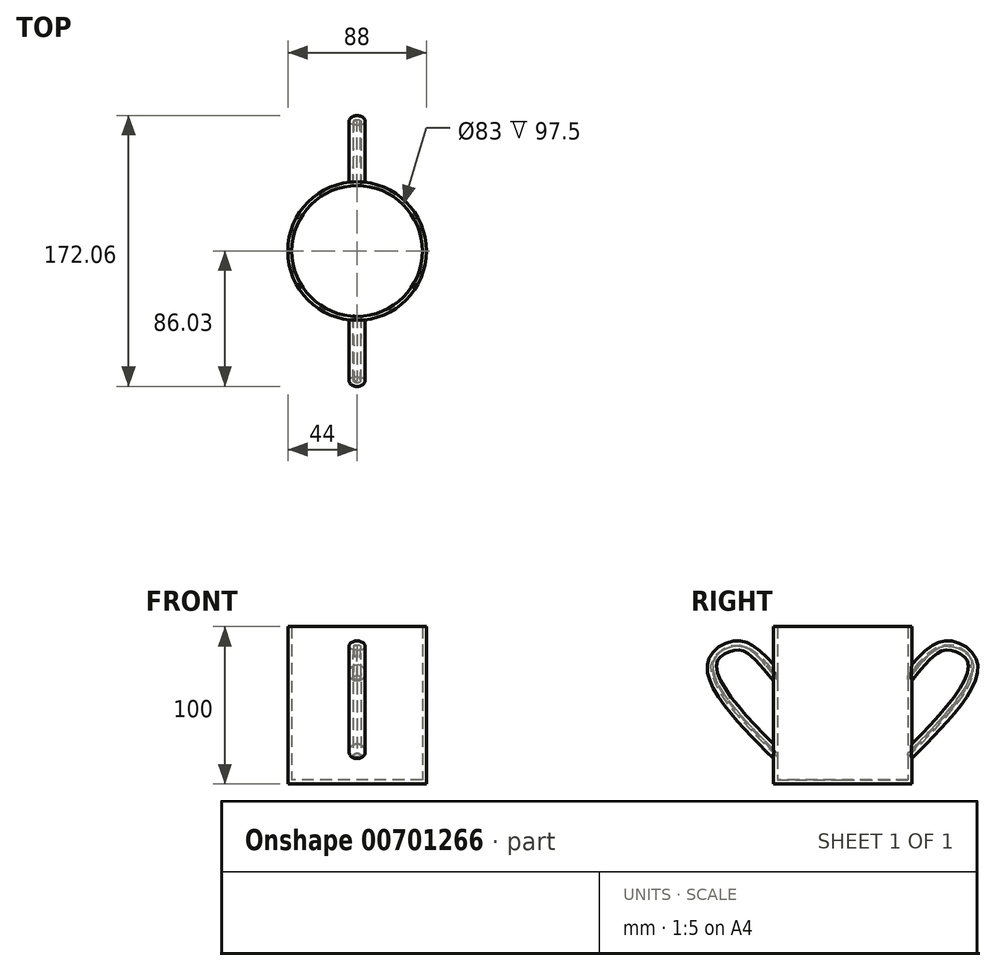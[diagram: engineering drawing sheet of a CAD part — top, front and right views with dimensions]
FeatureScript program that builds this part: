
annotation { "Feature Type Name" : "Feature", "Feature Type Description" : "" }
export const myFeature = defineFeature(function(context is Context, id is Id, definition is map)
    precondition{}
    {
        {
            var Q0;
            Q0=qCreatedBy(makeId("Top.planeOp"),FACE);
            var sketch = newSketch(context, id + "F0", { "sketchPlane" : qUnion([Q0])});
            skCircle(sketch, "E0", {"center": v(0, 0) * mm, "radius": 44 * mm});
            skSolve(sketch);
        }
        {
            var Q0;
            Q0=makeQuery(id+"F0.imprint","IMPRINT",FACE,{"disambiguationData":[TD([[makeQuery(id+"F0.imprint","IMPRINT",EDGE,{"derivedFrom":sQuery(id+"F0.wireOp",EDGE,"E0")}),1.0]])]});
            extrude(context, id + "F1", {"entities" : qUnion([Q0]), "depth" : 100 * mm, "offsetDistance" : 25 * mm});
        }
        {
            var Q0;
            Q0=qCreatedBy(makeId("Right.planeOp"),FACE);
            var sketch = newSketch(context, id + "F2", { "sketchPlane" : qUnion([Q0])});
            skFitSpline(sketch, "E1", {"points": [v(-41.77, 69.4) * mm, v(-65.9, 88.26) * mm, v(-83.21, 75.76) * mm, v(-41.33, 16.78) * mm], "startDerivative": vector(-76.5, 92.02) * mm, "endDerivative": vector(145.62, -147.3) * mm});
            skSolve(sketch);
        }
        {
            var Q0;
            Q0=qCreatedBy(makeId("Front.planeOp"),FACE);
            cPlane(context, id + "F3", {"entities" : qUnion([Q0]), "cplaneType" : CPlaneType.OFFSET, "offset" : 43.4 * mm, "width" : 150 * mm, "height" : 150 * mm});
        }
        {
            var Q0;
            Q0=qCreatedBy(id+"F3.planeOp",FACE);
            var sketch = newSketch(context, id + "F4", { "sketchPlane" : qUnion([Q0])});
            skCircle(sketch, "E2", {"center": v(0, 69.95) * mm, "radius": 5.12 * mm});
            skSolve(sketch);
        }
        {
            var Q0;
            Q0 = qSketchRegion(id + "F4", true);
            var Q1;
            Q1=sQuery(id+"F4.wireOp",EDGE,"E2");
            var Q2;
            Q2=sQuery(id+"F2.wireOp",EDGE,"E1");
            sweep(context, id + "F5", {"profiles" : qUnion([Q0]), "surfaceProfiles" : qUnion([Q1]), "path" : qUnion([Q2])});
        }
        {
            var Q0;
            Q0=makeQuery(id+"F5.opSweep","SWEPT_BODY",BODY,{"disambiguationData":[OSD([sQuery(id+"F2.wireOp",EDGE,"E1"),sQuery(id+"F4.wireOp",EDGE,"E2")])]});
            var Q1;
            Q1=qCreatedBy(makeId("Front.planeOp"),FACE);
            mirror(context, id + "F6", {"operationType" : NewBodyOperationType.ADD, "entities" : qUnion([Q0]), "mirrorPlane" : qUnion([Q1])});
        }
        {
            var Q0;
            Q0=makeQuery(id+"F1.opExtrude","CAP_FACE",FACE,{"disambiguationData":[OSD([sQuery(id+"F0.wireOp",EDGE,"E0")])],"isStart":false});
            shell(context, id + "F7", {"entities" : qUnion([Q0]), "thickness" : 2.5 * mm});
        }
    });
